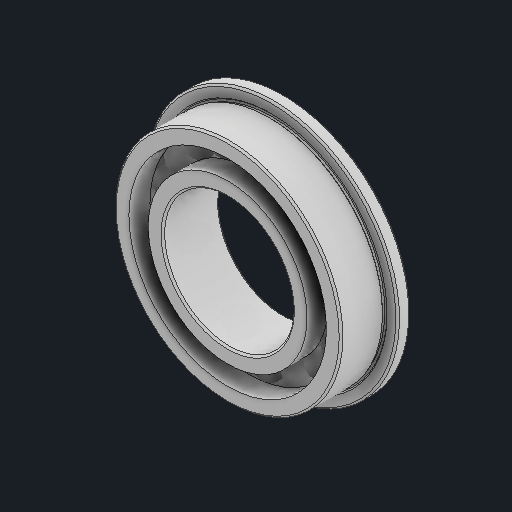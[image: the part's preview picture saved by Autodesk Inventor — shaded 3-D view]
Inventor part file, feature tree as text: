
AUTODESK INVENTOR PART (.ipt)
format: ipt  version: 2024 (Build 280153000, 153)  size: 834,560 bytes
history: native  units: in
note: dims shown in document units (in); Inventor stores cm internally (conversion verified against a paired STEP export)
features: other x18, fillet x2, revolve x1
ambient origin geometry x8: Origin, YZ Plane, XZ Plane, XY Plane, X Axis, Y Axis, Z Axis, Center Point
bodies: Solid1 (feature_tree), Solid2 (feature_tree), Solid3 (feature_tree), Solid4 (feature_tree), Solid5 (feature_tree), Solid6 (feature_tree), Solid7 (feature_tree), Solid8 (feature_tree), Solid9 (feature_tree), Solid10 (feature_tree), Solid11 (feature_tree), Solid12 (feature_tree), Solid13 (feature_tree), Solid14 (feature_tree), Solid15 (feature_tree), Solid16 (feature_tree), Solid17 (feature_tree), Solid18 (feature_tree), Solid19 (feature_tree), Solid20 (feature_tree), Solid21 (feature_tree)
feature tree (21):
  fillet  "Fillet1"  [1 undecoded]
  fillet  "Fillet2"  [1 undecoded]
  revolve  "Revolve3"  [1 undecoded]
  other  "CirPattern3[1]"
  other  "CirPattern3[2]"
  other  "CirPattern3[3]"
  other  "CirPattern3[4]"
  other  "CirPattern3[5]"
  other  "CirPattern3[6]"
  other  "CirPattern3[7]"
  other  "CirPattern3[8]"
  other  "CirPattern3[9]"
  other  "CirPattern3[10]"
  other  "CirPattern3[11]"
  other  "CirPattern3[12]"
  other  "CirPattern3[13]"
  other  "CirPattern3[14]"
  other  "CirPattern3[15]"
  other  "CirPattern3[16]"
  other  "CirPattern3[17]"
  other  "CirPattern3[18]"
note: 3 required parameter values undecoded (feature->parameter linkage not recoverable at this tier; creation-order binding heuristic only, values carry confidence <= 0.55)
